# Revit family: Shower-Column-Bradley_Corp-COL-3B
name_source: partatom
category: Plumbing Fixtures
revit_build: Autodesk Revit MEP 2012 (Build: 20110309_2315(x64)
units: mm (PartAtom-declared; Revit-internal decimal feet)

## types (1)
- Shower-Column-Bradley_Corp-COL-3B
    ADA Compliant = No
    Buy American Act = To Be Determined
    CWFU = 0
    Cold Water Connection Diameter = 1"
    Cold Water Connection Radius = 0"
    Column Material = Metal - Bradley Corp - Stainless Steel - Satin
    Depth = 12.338 "
    Description = 3-Person Column Beach Shower
    HWFU = 0
    Height = 78.25 "
    Hot Water Connection Diameter = 0"
    Hot Water Connection Radius = 0"
    Manufacturer = Bradley Corporation
    MasterFormat Number = 22 42 23
    MaterFormat Title = Commercial Showers
    Maximum Operating Pressure = 0.00 psi
    Minimum Flow = 0.0 GPM
    Model = COL-3B
    OmniClass Table 21 Number = 21-04 20 10 60
    OmniClass Table 21 Title = Plumbing Fixtures
    OmniClass Table 23 Number = 23-31 17 00
    OmniClass Table 23 Title = Showers
    Percentage of Recycled Content = 0
    Product Tech Data URL - English = http://bradleycorp.com
    Showerhead Height = 72 "
    Showerhead Material = Metal - Bradley Corp - Chrome
    Specifications URL = http://www.bradleycorp.com
    URL = http://www.bradleycorp.com
    Valve Material = Metal - Bradley Corp - Chrome
    Version = 2.0
    Width = 12.338 "

## geometry (parser evidence)
native form markers: Blend x6, Sweep x7
no freeform markers — native parametric forms only
